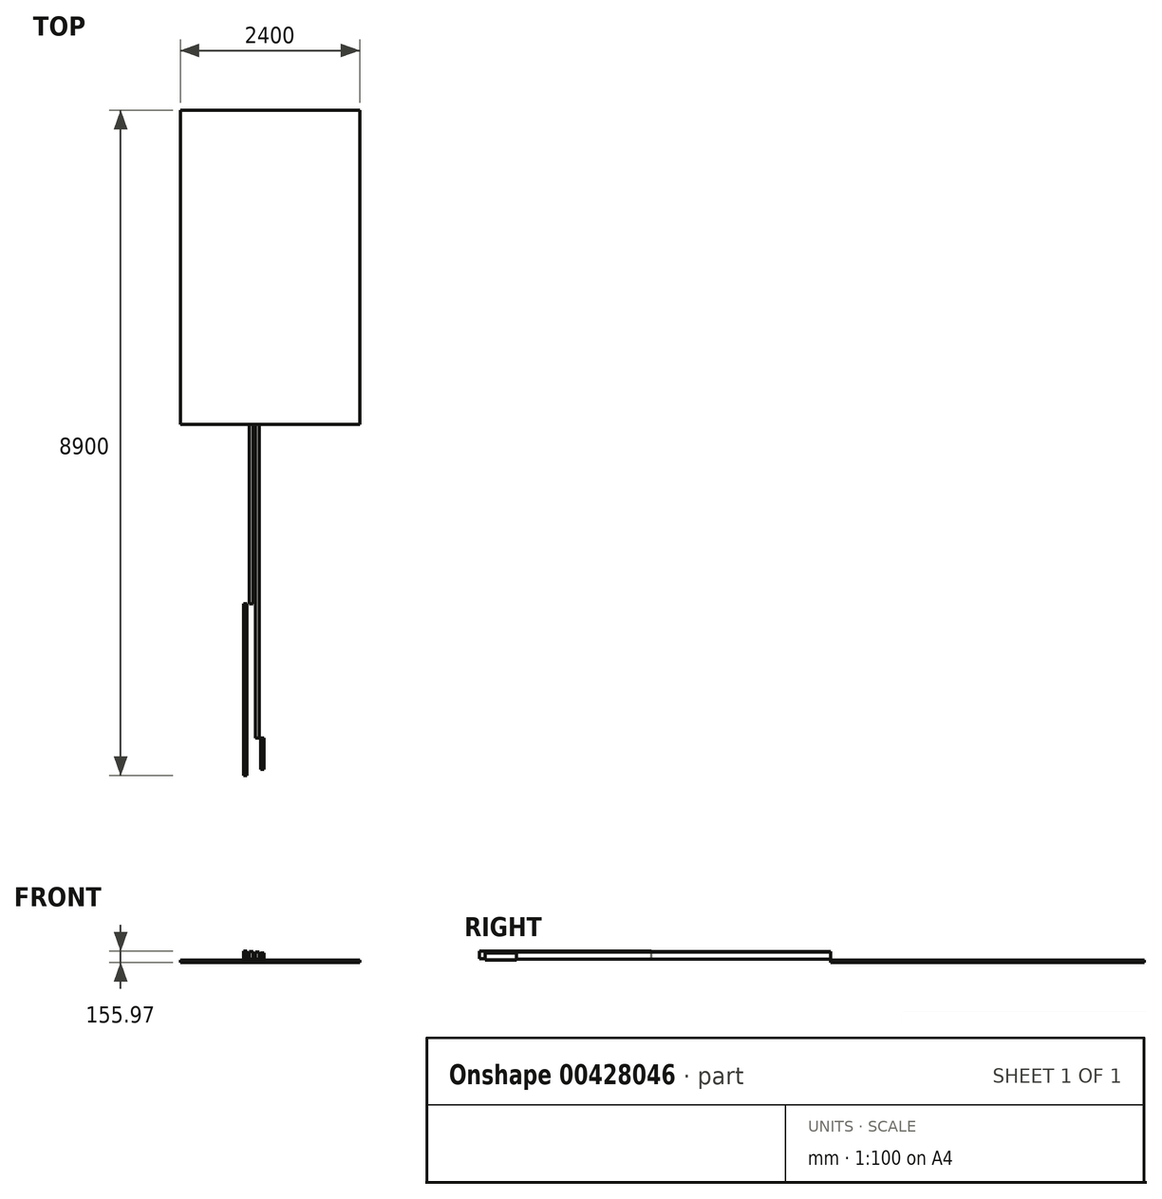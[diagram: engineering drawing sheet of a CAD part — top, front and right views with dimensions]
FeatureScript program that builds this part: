
annotation { "Feature Type Name" : "Feature", "Feature Type Description" : "" }
export const myFeature = defineFeature(function(context is Context, id is Id, definition is map)
    precondition{}
    {
        {
            var Q0;
            Q0=qCreatedBy(makeId("Top.planeOp"),FACE);
            var sketch = newSketch(context, id + "F0", { "sketchPlane" : qUnion([Q0])});
            skLineSegment(sketch, "E0.bottom", {"start": v(-1200, 2100) * mm, "end": v(1200, 2100) * mm});
            skLineSegment(sketch, "E0.top", {"start": v(-1200, -2100) * mm, "end": v(1200, -2100) * mm});
            skLineSegment(sketch, "E0.left", {"start": v(-1200, 2100) * mm, "end": v(-1200, -2100) * mm});
            skLineSegment(sketch, "E0.right", {"start": v(1200, 2100) * mm, "end": v(1200, -2100) * mm});
            skPoint(sketch, "E0.middle", {"position": v(0, 0) * mm});
            skSolve(sketch);
        }
        {
            var Q0;
            Q0 = qSketchRegion(id + "F0", true);
            extrude(context, id + "F1", {"entities" : qUnion([Q0]), "depth" : 10 * mm});
        }
        {
            var Q0;
            Q0=makeQuery(id+"F1.opExtrude","CAP_FACE",FACE,{"disambiguationData":[OSD([sQuery(id+"F0.wireOp",EDGE,"E0.bottom"),sQuery(id+"F0.wireOp",EDGE,"E0.top"),sQuery(id+"F0.wireOp",EDGE,"E0.left"),sQuery(id+"F0.wireOp",EDGE,"E0.right")])],"isStart":false});
            var sketch = newSketch(context, id + "F2", { "sketchPlane" : qUnion([Q0])});
            skSolve(sketch);
        }
        {
            var Q0;
            Q0=makeQuery(id+"F1.opExtrude","SWEPT_FACE",FACE,{"disambiguationData":[OSD([sQuery(id+"F0.wireOp",EDGE,"E0.top")])]});
            var sketch = newSketch(context, id + "F3", { "sketchPlane" : qUnion([Q0])});
            skLineSegment(sketch, "E1.bottom", {"start": v(-145, 43.68) * mm, "end": v(-195, 43.68) * mm});
            skLineSegment(sketch, "E1.top", {"start": v(-145, 143.68) * mm, "end": v(-195, 143.68) * mm});
            skLineSegment(sketch, "E1.left", {"start": v(-145, 43.68) * mm, "end": v(-145, 143.68) * mm});
            skLineSegment(sketch, "E1.right", {"start": v(-195, 43.68) * mm, "end": v(-195, 143.68) * mm});
            skSolve(sketch);
        }
        {
            var Q0;
            Q0=makeQuery(id+"F2.imprint","IMPRINT",FACE,{"disambiguationData":[TD([[makeQuery(id+"F2.imprint","IMPRINT",EDGE,{"derivedFrom":makeQuery(id+"F1.opExtrude","CAP_EDGE",EDGE,{"disambiguationData":[OSD([sQuery(id+"F0.wireOp",EDGE,"E0.bottom")])],"isStart":false})}),-1.0]])]});
            extrude(context, id + "F4", {"entities" : qUnion([Q0]), "operationType" : NewBodyOperationType.ADD, "depth" : 25 * mm});
        }
        {
            var Q0;
            Q0=makeQuery(id+"F3.imprint","IMPRINT",FACE,{"disambiguationData":[TD([[makeQuery(id+"F3.imprint","IMPRINT",EDGE,{"derivedFrom":sQuery(id+"F3.wireOp",EDGE,"E1.bottom")}),-1.0]])]});
            var sketch = newSketch(context, id + "F5", { "sketchPlane" : qUnion([Q0])});
            skSolve(sketch);
        }
        {
            var Q0;
            Q0=makeQuery(id+"F3.imprint","IMPRINT",FACE,{"disambiguationData":[TD([[makeQuery(id+"F3.imprint","IMPRINT",EDGE,{"derivedFrom":sQuery(id+"F3.wireOp",EDGE,"E1.bottom")}),-1.0]])]});
            extrude(context, id + "F6", {"entities" : qUnion([Q0]), "depth" : 4200 * mm});
        }
        {
            var Q0;
            Q0=makeQuery(id+"F5.imprint","IMPRINT",FACE,{"disambiguationData":[TD([[makeQuery(id+"F5.imprint","IMPRINT",EDGE,{"derivedFrom":makeQuery(id+"F3.imprint","IMPRINT",EDGE,{"derivedFrom":sQuery(id+"F3.wireOp",EDGE,"E1.bottom")})}),-1.0]])]});
            var sketch = newSketch(context, id + "F7", { "sketchPlane" : qUnion([Q0])});
            skLineSegment(sketch, "E2.bottom", {"start": v(-228.53, 148.07) * mm, "end": v(-278.53, 148.07) * mm});
            skLineSegment(sketch, "E2.top", {"start": v(-228.53, 48.07) * mm, "end": v(-278.53, 48.07) * mm});
            skLineSegment(sketch, "E2.left", {"start": v(-228.53, 148.07) * mm, "end": v(-228.53, 48.07) * mm});
            skLineSegment(sketch, "E2.right", {"start": v(-278.53, 148.07) * mm, "end": v(-278.53, 48.07) * mm});
            skSolve(sketch);
        }
        {
            var Q0;
            Q0 = qSketchRegion(id + "F7", true);
            extrude(context, id + "F8", {"entities" : qUnion([Q0]), "depth" : 2400 * mm});
        }
        {
            var Q0;
            Q0=makeQuery(id+"F6.opExtrude","CAP_FACE",FACE,{"disambiguationData":[OSD([sQuery(id+"F3.wireOp",EDGE,"E1.bottom"),sQuery(id+"F3.wireOp",EDGE,"E1.top"),sQuery(id+"F3.wireOp",EDGE,"E1.left"),sQuery(id+"F3.wireOp",EDGE,"E1.right")])],"isStart":false});
            var sketch = newSketch(context, id + "F9", { "sketchPlane" : qUnion([Q0])});
            skLineSegment(sketch, "E3.bottom", {"start": v(-128.2, 131.77) * mm, "end": v(-78.2, 131.77) * mm});
            skLineSegment(sketch, "E3.top", {"start": v(-128.2, 31.77) * mm, "end": v(-78.2, 31.77) * mm});
            skLineSegment(sketch, "E3.left", {"start": v(-128.2, 131.77) * mm, "end": v(-128.2, 31.77) * mm});
            skLineSegment(sketch, "E3.right", {"start": v(-78.2, 131.77) * mm, "end": v(-78.2, 31.77) * mm});
            skSolve(sketch);
        }
        {
            var Q0;
            Q0=makeQuery(id+"F9.imprint","IMPRINT",FACE,{"disambiguationData":[TD([[makeQuery(id+"F9.imprint","IMPRINT",EDGE,{"derivedFrom":sQuery(id+"F9.wireOp",EDGE,"E3.bottom")}),-1.0]])]});
            extrude(context, id + "F10", {"entities" : qUnion([Q0]), "depth" : 420 * mm});
        }
        {
            var Q0;
            Q0=makeQuery(id+"F8.opExtrude","CAP_FACE",FACE,{"disambiguationData":[OSD([sQuery(id+"F7.wireOp",EDGE,"E2.bottom"),sQuery(id+"F7.wireOp",EDGE,"E2.top"),sQuery(id+"F7.wireOp",EDGE,"E2.left"),sQuery(id+"F7.wireOp",EDGE,"E2.right")])],"isStart":false});
            var sketch = newSketch(context, id + "F11", { "sketchPlane" : qUnion([Q0])});
            skLineSegment(sketch, "E4.bottom", {"start": v(-356.02, 55.97) * mm, "end": v(-306.02, 55.97) * mm});
            skLineSegment(sketch, "E4.top", {"start": v(-356.02, 155.97) * mm, "end": v(-306.02, 155.97) * mm});
            skLineSegment(sketch, "E4.left", {"start": v(-356.02, 55.97) * mm, "end": v(-356.02, 155.97) * mm});
            skLineSegment(sketch, "E4.right", {"start": v(-306.02, 55.97) * mm, "end": v(-306.02, 155.97) * mm});
            skSolve(sketch);
        }
        {
            var Q0;
            Q0 = qSketchRegion(id + "F11", true);
            extrude(context, id + "F12", {"entities" : qUnion([Q0]), "depth" : 2300 * mm});
        }
    });
